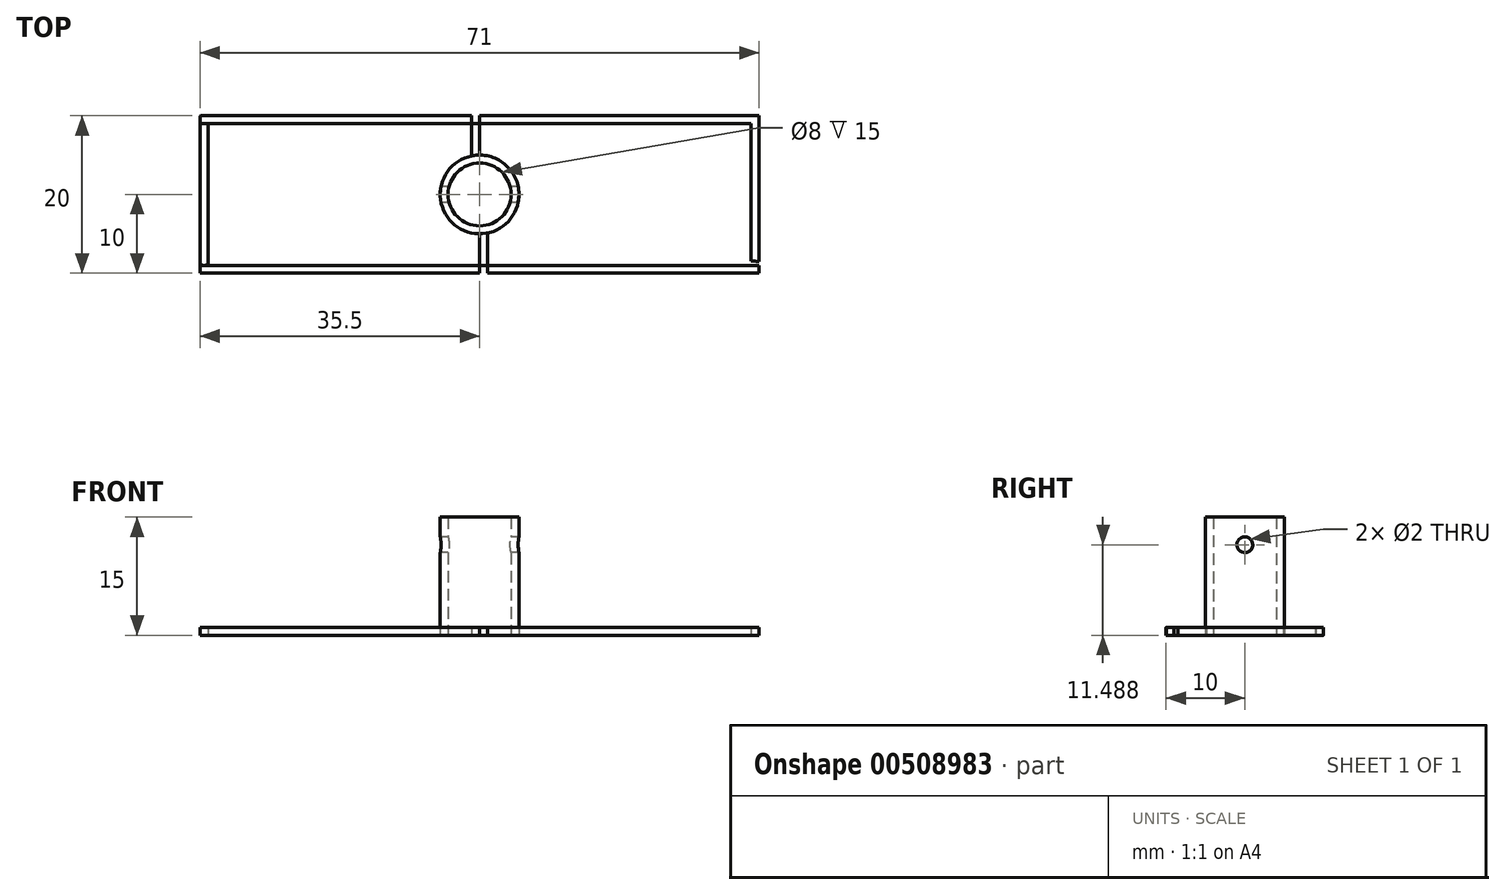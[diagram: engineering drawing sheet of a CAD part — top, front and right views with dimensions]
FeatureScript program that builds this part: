
annotation { "Feature Type Name" : "Feature", "Feature Type Description" : "" }
export const myFeature = defineFeature(function(context is Context, id is Id, definition is map)
    precondition{}
    {
        {
            var Q0;
            Q0=qCreatedBy(makeId("Top.planeOp"),FACE);
            var sketch = newSketch(context, id + "F0", { "sketchPlane" : qUnion([Q0])});
            skLineSegment(sketch, "E0.bottom", {"start": v(-35, 10) * mm, "end": v(35, 10) * mm});
            skLineSegment(sketch, "E0.top", {"start": v(-35, -10) * mm, "end": v(35, -10) * mm});
            skPoint(sketch, "E0.middle", {"position": v(0, 0) * mm});
            skArc(sketch, "E1", {"start": v(-35, 10) * mm, "mid": v(-45, 0) * mm, "end": v(-35, -10) * mm});
            skArc(sketch, "E2", {"start": v(35, -10) * mm, "mid": v(45, 0) * mm, "end": v(35, 10) * mm});
            skLineSegment(sketch, "E3.bottom", {"start": v(-35.5, 9.99) * mm, "end": v(-34.5, 9.99) * mm});
            skLineSegment(sketch, "E3.top", {"start": v(-35.5, -9.99) * mm, "end": v(-34.5, -9.99) * mm});
            skLineSegment(sketch, "E3.left", {"start": v(-35.5, 9.99) * mm, "end": v(-35.5, -9.99) * mm});
            skLineSegment(sketch, "E3.right", {"start": v(-34.5, 9.99) * mm, "end": v(-34.5, -9.99) * mm});
            skLineSegment(sketch, "E4.bottom", {"start": v(34.5, 10) * mm, "end": v(35.5, 10) * mm});
            skLineSegment(sketch, "E4.top", {"start": v(34.5, -10) * mm, "end": v(35.5, -10) * mm});
            skLineSegment(sketch, "E4.left", {"start": v(34.5, 10) * mm, "end": v(34.5, -10) * mm});
            skLineSegment(sketch, "E4.right", {"start": v(35.5, 10) * mm, "end": v(35.5, -10) * mm});
            skPoint(sketch, "E5.oppositeSnap0", {"position": v(0, 10) * mm});
            skLineSegment(sketch, "E5.bottom", {"start": v(-1, 10) * mm, "end": v(0, 10) * mm});
            skLineSegment(sketch, "E5.top", {"start": v(-1, 6) * mm, "end": v(0, 6) * mm});
            skLineSegment(sketch, "E5.left", {"start": v(-1, 10) * mm, "end": v(-1, 6) * mm});
            skLineSegment(sketch, "E5.right", {"start": v(0, 10) * mm, "end": v(0, 6) * mm});
            skLineSegment(sketch, "E6.bottom", {"start": v(0, -6) * mm, "end": v(1, -6) * mm});
            skLineSegment(sketch, "E6.top", {"start": v(0, -10) * mm, "end": v(1, -10) * mm});
            skLineSegment(sketch, "E6.left", {"start": v(0, -6) * mm, "end": v(0, -10) * mm});
            skLineSegment(sketch, "E6.right", {"start": v(1, -6) * mm, "end": v(1, -10) * mm});
            skLineSegment(sketch, "E7.bottom", {"start": v(-35.5, 9) * mm, "end": v(35.5, 9) * mm});
            skLineSegment(sketch, "E7.top", {"start": v(-35.5, -9) * mm, "end": v(35.5, -9) * mm});
            skLineSegment(sketch, "E7.left", {"start": v(-35.5, 9) * mm, "end": v(-35.5, -9) * mm});
            skLineSegment(sketch, "E7.right", {"start": v(35.5, 9) * mm, "end": v(35.5, -9) * mm});
            skArc(sketch, "E8", {"start": v(34.5, -8.44) * mm, "mid": v(44, 0) * mm, "end": v(34.5, 8.44) * mm});
            skArc(sketch, "E9", {"start": v(-34.5, 8.99) * mm, "mid": v(-44, 0) * mm, "end": v(-34.5, -8.99) * mm});
            skCircle(sketch, "E10", {"center": v(0, 0) * mm, "radius": 5 * mm});
            skLineSegment(sketch, "E11", {"start": v(-1, 6) * mm, "end": v(-1, 4.9) * mm});
            skLineSegment(sketch, "E12", {"start": v(0, 6) * mm, "end": v(0, 5) * mm});
            skLineSegment(sketch, "E13", {"start": v(1, -6) * mm, "end": v(1, -4.9) * mm});
            skLineSegment(sketch, "E14", {"start": v(0, -6) * mm, "end": v(0, -5) * mm});
            skCircle(sketch, "E15", {"center": v(0, 0) * mm, "radius": 4 * mm});
            skSolve(sketch);
        }
        {
            var Q0;
            {var subQ1=sQuery(id+"F0.wireOp",EDGE,"E3.bottom");Q0=makeQuery(id+"F0.imprint","IMPRINT",FACE,{"disambiguationData":[TD([[makeQuery(id+"F0.imprint","IMPRINT",EDGE,{"derivedFrom":subQ1}),1.0]])]});}
            var Q1;
            {var subQ5=sQuery(id+"F0.wireOp",EDGE,"E3.bottom");Q1=makeQuery(id+"F0.imprint","IMPRINT",FACE,{"disambiguationData":[TD([[makeQuery(id+"F0.imprint","IMPRINT",EDGE,{"derivedFrom":subQ5}),-1.0]])]});}
            var Q2;
            {var subQ0=sQuery(id+"F0.wireOp",EDGE,"E7.left");var subQ3=sQuery(id+"F0.wireOp",EDGE,"E9");var subQ4=makeQuery(id+"F0.imprint","INTERSECT",VERTEX,{"disambiguationData":[OD(0.0)],"derivedFrom":[subQ0,subQ3]});Q2=makeQuery(id+"F0.imprint","IMPRINT",FACE,{"disambiguationData":[TD([[makeQuery(id+"F0.imprint","IMPRINT",EDGE,{"disambiguationData":[TD([[subQ4,-1.0]])],"derivedFrom":subQ3}),-1.0]])]});}
            var Q3;
            {var subQ5=sQuery(id+"F0.wireOp",EDGE,"E3.top");Q3=makeQuery(id+"F0.imprint","IMPRINT",FACE,{"disambiguationData":[TD([[makeQuery(id+"F0.imprint","IMPRINT",EDGE,{"derivedFrom":subQ5}),1.0]])]});}
            var Q4;
            {var subQ1=sQuery(id+"F0.wireOp",EDGE,"E3.top");Q4=makeQuery(id+"F0.imprint","IMPRINT",FACE,{"disambiguationData":[TD([[makeQuery(id+"F0.imprint","IMPRINT",EDGE,{"derivedFrom":subQ1}),-1.0]])]});}
            var Q5;
            {var subQ0=sQuery(id+"F0.wireOp",EDGE,"E4.left");var subQ5=sQuery(id+"F0.wireOp",EDGE,"E7.top");var subQ7=makeQuery(id+"F0.imprint","INTERSECT",VERTEX,{"derivedFrom":[subQ0,subQ5]});Q5=makeQuery(id+"F0.imprint","IMPRINT",FACE,{"disambiguationData":[TD([[makeQuery(id+"F0.imprint","IMPRINT",EDGE,{"disambiguationData":[TD([[subQ7,1.0]])],"derivedFrom":subQ5}),-1.0]])]});}
            var Q6;
            {var subQ0=sQuery(id+"F0.wireOp",EDGE,"E6.top");Q6=makeQuery(id+"F0.imprint","IMPRINT",FACE,{"disambiguationData":[TD([[makeQuery(id+"F0.imprint","IMPRINT",EDGE,{"derivedFrom":subQ0}),1.0]])]});}
            var Q7;
            {var subQ3=sQuery(id+"F0.wireOp",EDGE,"E2");var subQ6=sQuery(id+"F0.wireOp",EDGE,"E4.top");var subQ8=makeQuery(id+"F0.imprint","INTERSECT",VERTEX,{"derivedFrom":[subQ3,subQ6]});Q7=makeQuery(id+"F0.imprint","IMPRINT",FACE,{"disambiguationData":[TD([[makeQuery(id+"F0.imprint","IMPRINT",EDGE,{"disambiguationData":[TD([[subQ8,-1.0]])],"derivedFrom":subQ3}),1.0]])]});}
            var Q8;
            {var subQ1=sQuery(id+"F0.wireOp",EDGE,"E4.right");var subQ3=sQuery(id+"F0.wireOp",EDGE,"E2");var subQ4=makeQuery(id+"F0.imprint","INTERSECT",VERTEX,{"disambiguationData":[OD(0.0)],"derivedFrom":[subQ3,subQ1]});Q8=makeQuery(id+"F0.imprint","IMPRINT",FACE,{"disambiguationData":[TD([[makeQuery(id+"F0.imprint","IMPRINT",EDGE,{"disambiguationData":[TD([[subQ4,-1.0]])],"derivedFrom":subQ3}),1.0]])]});}
            var Q9;
            {var subQ0=sQuery(id+"F0.wireOp",EDGE,"E4.left");var subQ5=sQuery(id+"F0.wireOp",EDGE,"E7.bottom");var subQ7=makeQuery(id+"F0.imprint","INTERSECT",VERTEX,{"derivedFrom":[subQ0,subQ5]});Q9=makeQuery(id+"F0.imprint","IMPRINT",FACE,{"disambiguationData":[TD([[makeQuery(id+"F0.imprint","IMPRINT",EDGE,{"disambiguationData":[TD([[subQ7,1.0]])],"derivedFrom":subQ5}),1.0]])]});}
            var Q10;
            {var subQ1=sQuery(id+"F0.wireOp",EDGE,"E4.bottom");var subQ7=sQuery(id+"F0.wireOp",EDGE,"E2");var subQ9=makeQuery(id+"F0.imprint","INTERSECT",VERTEX,{"derivedFrom":[subQ7,subQ1]});Q10=makeQuery(id+"F0.imprint","IMPRINT",FACE,{"disambiguationData":[TD([[makeQuery(id+"F0.imprint","IMPRINT",EDGE,{"disambiguationData":[TD([[subQ9,1.0]])],"derivedFrom":subQ7}),1.0]])]});}
            var Q11;
            {var subQ0=sQuery(id+"F0.wireOp",EDGE,"E8");var subQ1=sQuery(id+"F0.wireOp",EDGE,"E4.left");var subQ2=makeQuery(id+"F0.imprint","INTERSECT",VERTEX,{"disambiguationData":[OD(0.0)],"derivedFrom":[subQ1,subQ0]});Q11=makeQuery(id+"F0.imprint","IMPRINT",FACE,{"disambiguationData":[TD([[makeQuery(id+"F0.imprint","IMPRINT",EDGE,{"disambiguationData":[TD([[subQ2,1.0]])],"derivedFrom":subQ1}),1.0]])]});}
            var Q12;
            {var subQ0=sQuery(id+"F0.wireOp",EDGE,"E8");var subQ1=sQuery(id+"F0.wireOp",EDGE,"E4.left");var subQ2=makeQuery(id+"F0.imprint","INTERSECT",VERTEX,{"disambiguationData":[OD(1.0)],"derivedFrom":[subQ1,subQ0]});Q12=makeQuery(id+"F0.imprint","IMPRINT",FACE,{"disambiguationData":[TD([[makeQuery(id+"F0.imprint","IMPRINT",EDGE,{"disambiguationData":[TD([[subQ2,1.0]])],"derivedFrom":subQ1}),1.0]])]});}
            var Q13;
            {var subQ0=sQuery(id+"F0.wireOp",EDGE,"E9");var subQ1=sQuery(id+"F0.wireOp",EDGE,"E3.right");var subQ2=makeQuery(id+"F0.imprint","INTERSECT",VERTEX,{"disambiguationData":[OD(0.0)],"derivedFrom":[subQ1,subQ0]});Q13=makeQuery(id+"F0.imprint","IMPRINT",FACE,{"disambiguationData":[TD([[makeQuery(id+"F0.imprint","IMPRINT",EDGE,{"disambiguationData":[TD([[subQ2,-1.0]])],"derivedFrom":subQ1}),-1.0]])]});}
            var Q14;
            {var subQ0=sQuery(id+"F0.wireOp",EDGE,"E6.bottom");Q14=makeQuery(id+"F0.imprint","IMPRINT",FACE,{"disambiguationData":[TD([[makeQuery(id+"F0.imprint","IMPRINT",EDGE,{"derivedFrom":subQ0}),-1.0]])]});}
            var Q15;
            {var subQ0=sQuery(id+"F0.wireOp",EDGE,"E5.top");Q15=makeQuery(id+"F0.imprint","IMPRINT",FACE,{"disambiguationData":[TD([[makeQuery(id+"F0.imprint","IMPRINT",EDGE,{"derivedFrom":subQ0}),1.0]])]});}
            var Q16;
            {var subQ0=sQuery(id+"F0.wireOp",EDGE,"E5.bottom");Q16=makeQuery(id+"F0.imprint","IMPRINT",FACE,{"disambiguationData":[TD([[makeQuery(id+"F0.imprint","IMPRINT",EDGE,{"derivedFrom":subQ0}),-1.0]])]});}
            var Q17;
            {var subQ0=sQuery(id+"F0.wireOp",EDGE,"E8");var subQ1=sQuery(id+"F0.wireOp",EDGE,"E4.left");var subQ2=makeQuery(id+"F0.imprint","INTERSECT",VERTEX,{"disambiguationData":[OD(0.0)],"derivedFrom":[subQ1,subQ0]});Q17=makeQuery(id+"F0.imprint","IMPRINT",FACE,{"disambiguationData":[TD([[makeQuery(id+"F0.imprint","IMPRINT",EDGE,{"disambiguationData":[TD([[subQ2,-1.0]])],"derivedFrom":subQ1}),1.0]])]});}
            var Q18;
            Q18=makeQuery(id+"F0.imprint","IMPRINT",FACE,{"disambiguationData":[TD([[makeQuery(id+"F0.imprint","IMPRINT",EDGE,{"derivedFrom":sQuery(id+"F0.wireOp",EDGE,"E10")}),-1.0]])]});
            extrude(context, id + "F1", {"entities" : qUnion([Q0, Q1, Q2, Q3, Q4, Q5, Q6, Q7, Q8, Q9, Q10, Q11, Q12, Q13, Q14, Q15, Q16, Q17, Q18]), "depth" : 1 * mm});
        }
        {
            var Q0;
            Q0=makeQuery(id+"F0.imprint","IMPRINT",FACE,{"disambiguationData":[TD([[makeQuery(id+"F0.imprint","IMPRINT",EDGE,{"derivedFrom":sQuery(id+"F0.wireOp",EDGE,"E15")}),-1.0]])]});
            extrude(context, id + "F2", {"entities" : qUnion([Q0]), "operationType" : NewBodyOperationType.ADD, "depth" : 15 * mm});
        }
        {
            var Q0;
            Q0=qCreatedBy(makeId("Right.planeOp"),FACE);
            var sketch = newSketch(context, id + "F3", { "sketchPlane" : qUnion([Q0])});
            skCircle(sketch, "E16", {"center": v(0, 11.49) * mm, "radius": 1 * mm});
            skSolve(sketch);
        }
        {
            var Q0;
            Q0 = qSketchRegion(id + "F3", true);
            extrude(context, id + "F4", {"entities" : qUnion([Q0]), "operationType" : NewBodyOperationType.REMOVE, "endBound" : BoundingType.SYMMETRIC, "depth" : 25 * mm});
        }
    });
